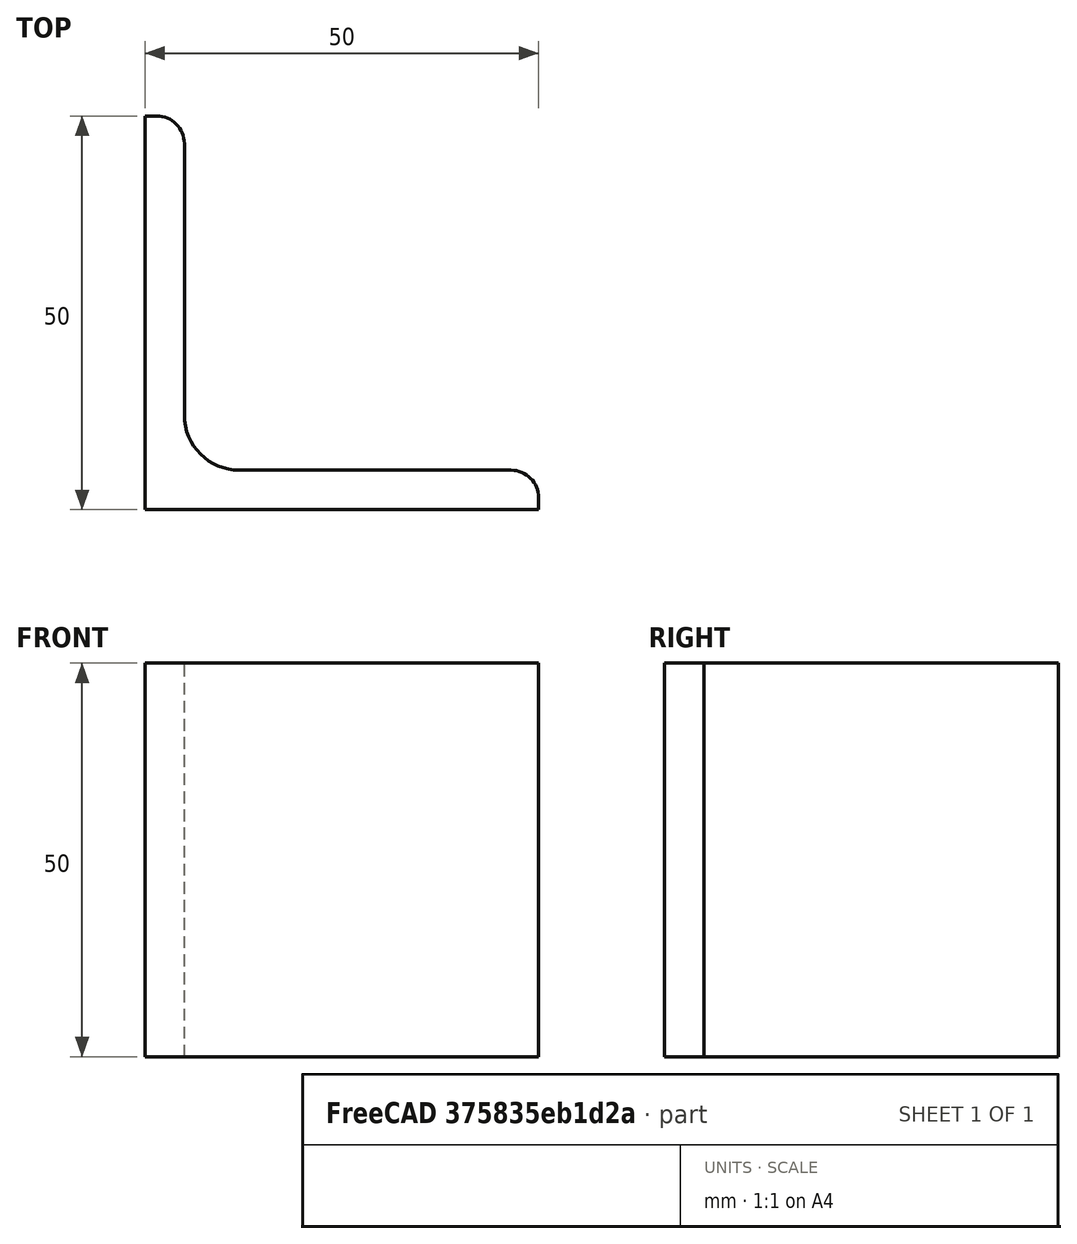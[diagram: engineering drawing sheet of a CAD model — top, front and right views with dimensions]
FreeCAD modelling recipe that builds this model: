
FCSTD DOCUMENT  (FreeCAD 0.15R4671 (Git))
Label: Angle Bar L50x50x5 EN10056 S235JR
License: All rights reserved
LicenseURL: http://en.wikipedia.org/wiki/All_rights_reserved
objects: Sketcher::SketchObject×1, Part::Extrusion×1
note: 2 computed .brp shape members not serialized (recipe doc carries the construction recipe); baked Part::Feature solids carry a one-line shape summary decoded from their .brp

FEATURE [Sketcher::SketchObject] Sketch
  sketch-geometry (9):
    g0: LineSegment StartX=0 StartY=0 StartZ=0 EndX=50 EndY=0 EndZ=0
    g1: LineSegment StartX=50 StartY=0 StartZ=0 EndX=50 EndY=1.5 EndZ=0
    g2: LineSegment StartX=46.5 StartY=5 StartZ=0 EndX=12 EndY=5 EndZ=0
    g3: LineSegment StartX=0 StartY=0 StartZ=0 EndX=0 EndY=50 EndZ=0
    g4: LineSegment StartX=0 StartY=50 StartZ=0 EndX=1.5 EndY=50 EndZ=0
    g5: LineSegment StartX=5 StartY=46.5 StartZ=0 EndX=5 EndY=12 EndZ=0
    g6: ArcOfCircle CenterX=12 CenterY=12 CenterZ=0 NormalX=0 NormalY=0 NormalZ=1 Radius=7 StartAngle=3.14159 EndAngle=4.71239
    g7: ArcOfCircle CenterX=1.5 CenterY=46.5 CenterZ=0 NormalX=0 NormalY=0 NormalZ=1 Radius=3.5 StartAngle=0 EndAngle=1.5708
    g8: ArcOfCircle CenterX=46.5 CenterY=1.5 CenterZ=0 NormalX=0 NormalY=0 NormalZ=1 Radius=3.5 StartAngle=0 EndAngle=1.5708
  constraints (23):
    c: Coincident(g0,g-1)
    c: Horizontal(g0)
    c: Coincident(g1,g0)
    c: Vertical(g1)
    c: Horizontal(g2)
    c: Coincident(g3,g-1)
    c: Vertical(g3)
    c: Coincident(g4,g3)
    c: Horizontal(g4)
    c: Vertical(g5)
    c: Tangent(g5,g6) = -1.5708
    c: Tangent(g2,g6) = 1.5708
    c: Tangent(g4,g7) = 1.5708
    c: Tangent(g5,g7) = 1.5708
    c: Tangent(g2,g8) = -1.5708
    c: Tangent(g1,g8) = -1.5708
    c: DistanceX(g0) = 50
    c: DistanceY(g3) = 50
    c: DistanceY(g0,g2) = 5
    c: DistanceX(g3,g5) = 5
    c: Radius(g6) = 7
    c: Radius(g8) = 3.5
    c: Radius(g7) = 3.5
FEATURE [Part::Extrusion] Extrude  label="Angle Bar L50x50x5 EN10056 S235JR"
  Base = -> Sketch
  Dir = (0,0,50)
  Solid = true
